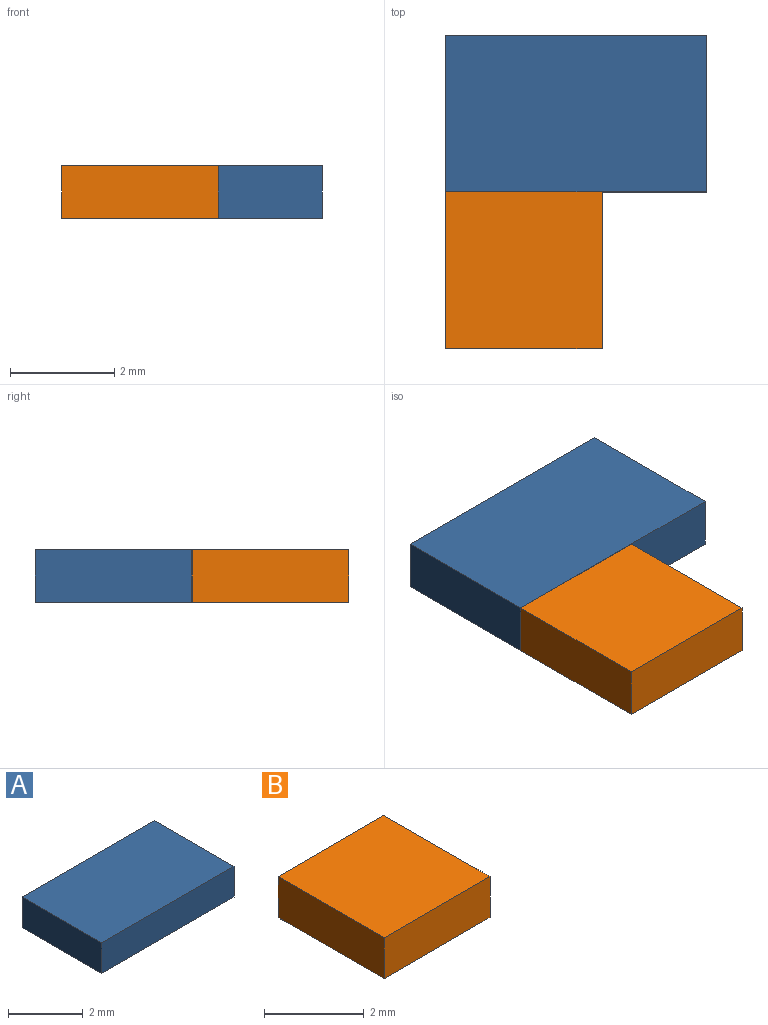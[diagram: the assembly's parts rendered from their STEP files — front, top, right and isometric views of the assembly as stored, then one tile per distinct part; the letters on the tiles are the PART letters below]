
ASSEMBLY  parts=2 mates=1
PART A: 6 faces, bbox 5x3x1 mm
  f0: plane 5x1mm, normal (0,-1,0), area 5mm2, adj f1,f3,f4,f5
  f1: plane 3x1mm, normal (1,0,0), area 3mm2, adj f0,f2,f4,f5
  f2: plane 5x1mm, normal (0,1,0), area 5mm2, adj f1,f3,f4,f5
  f3: plane 3x1mm, normal (-1,0,0), area 3mm2, adj f0,f2,f4,f5
  f4: plane 5x3mm, normal (0,0,1), area 15mm2, adj f0,f1,f2,f3
  f5: plane 5x3mm, normal (0,0,-1), area 15mm2, adj f0,f1,f2,f3
PART B: 6 faces, bbox 3x3x1 mm
  f0: plane 3x1mm, normal (0,-1,0), area 3mm2, adj f1,f3,f4,f5
  f1: plane 3x1mm, normal (1,0,0), area 3mm2, adj f0,f2,f4,f5
  f2: plane 3x1mm, normal (0,1,0), area 3mm2, adj f1,f3,f4,f5
  f3: plane 3x1mm, normal (-1,0,0), area 3mm2, adj f0,f2,f4,f5
  f4: plane 3x3mm, normal (0,0,1), area 9mm2, adj f0,f1,f2,f3
  f5: plane 3x3mm, normal (0,0,-1), area 9mm2, adj f0,f1,f2,f3
PLACE A t=(10.28,29.27,13.47)mm
PLACE B t=(10.28,26.27,13.47)mm
MATE fastened B.f4 <-> A.f4  axis (0,0,1) through (-51.55,-8.94,14.47)mm
